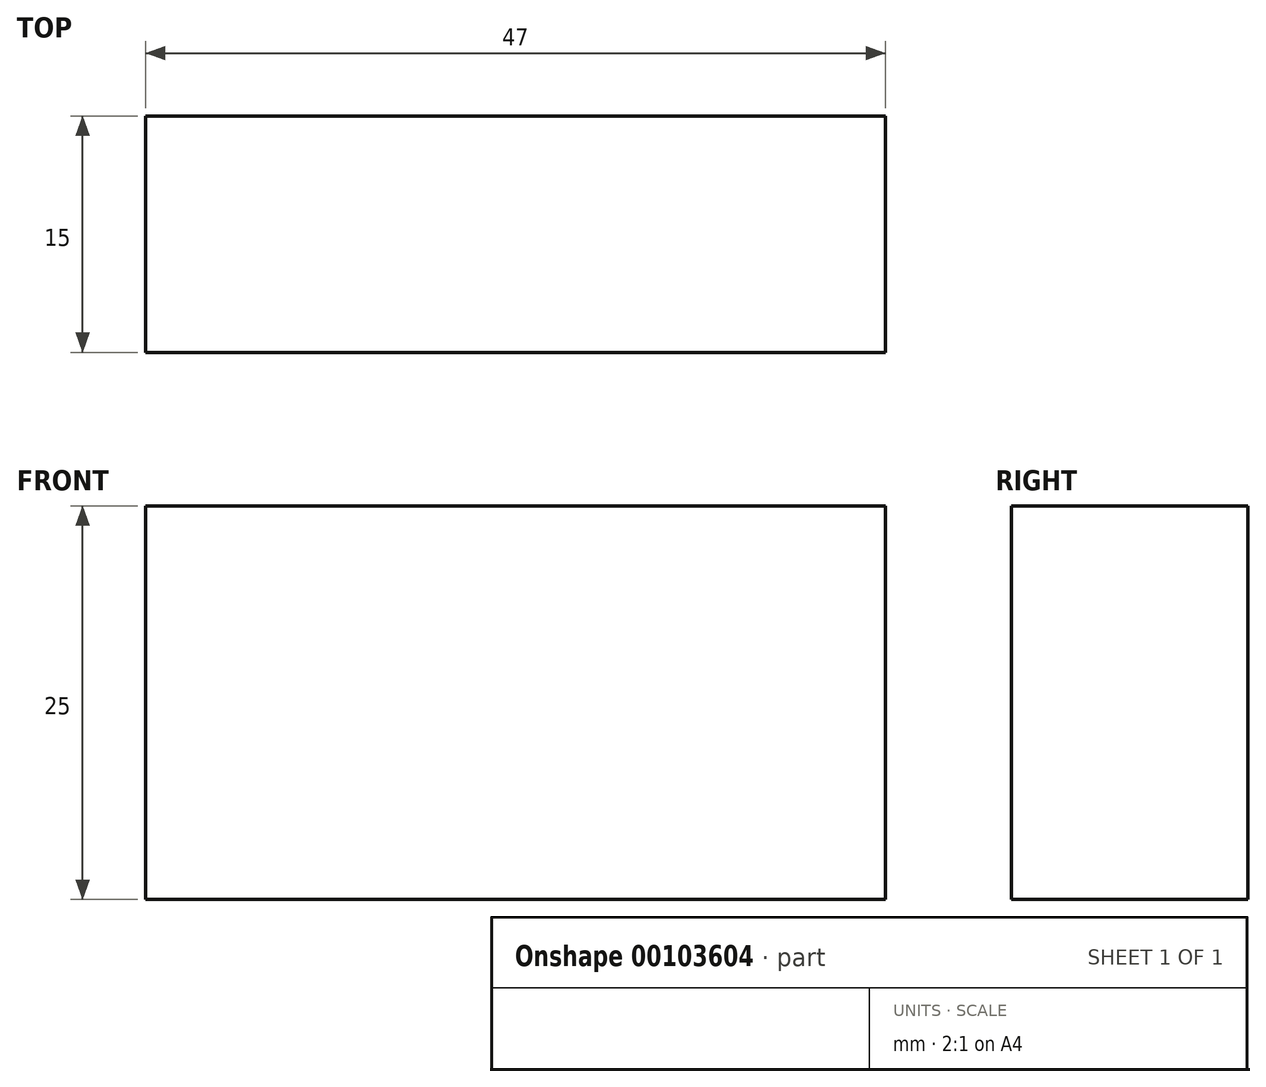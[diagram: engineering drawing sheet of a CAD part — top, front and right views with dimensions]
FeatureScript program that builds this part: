
annotation { "Feature Type Name" : "Feature", "Feature Type Description" : "" }
export const myFeature = defineFeature(function(context is Context, id is Id, definition is map)
    precondition{}
    {
        {
            var Q0;
            Q0=qCreatedBy(makeId("Front.planeOp"),FACE);
            var sketch = newSketch(context, id + "F0", { "sketchPlane" : qUnion([Q0])});
            skLineSegment(sketch, "E0.bottom", {"start": v(-24.17, 12.3) * mm, "end": v(22.83, 12.3) * mm});
            skLineSegment(sketch, "E0.top", {"start": v(-24.17, -12.7) * mm, "end": v(22.83, -12.7) * mm});
            skLineSegment(sketch, "E0.left", {"start": v(-24.17, 12.3) * mm, "end": v(-24.17, -12.7) * mm});
            skLineSegment(sketch, "E0.right", {"start": v(22.83, 12.3) * mm, "end": v(22.83, -12.7) * mm});
            skSolve(sketch);
        }
        {
            var Q0;
            Q0 = qSketchRegion(id + "F0", true);
            extrude(context, id + "F1", {"entities" : qUnion([Q0]), "depth" : 15 * mm});
        }
    });
